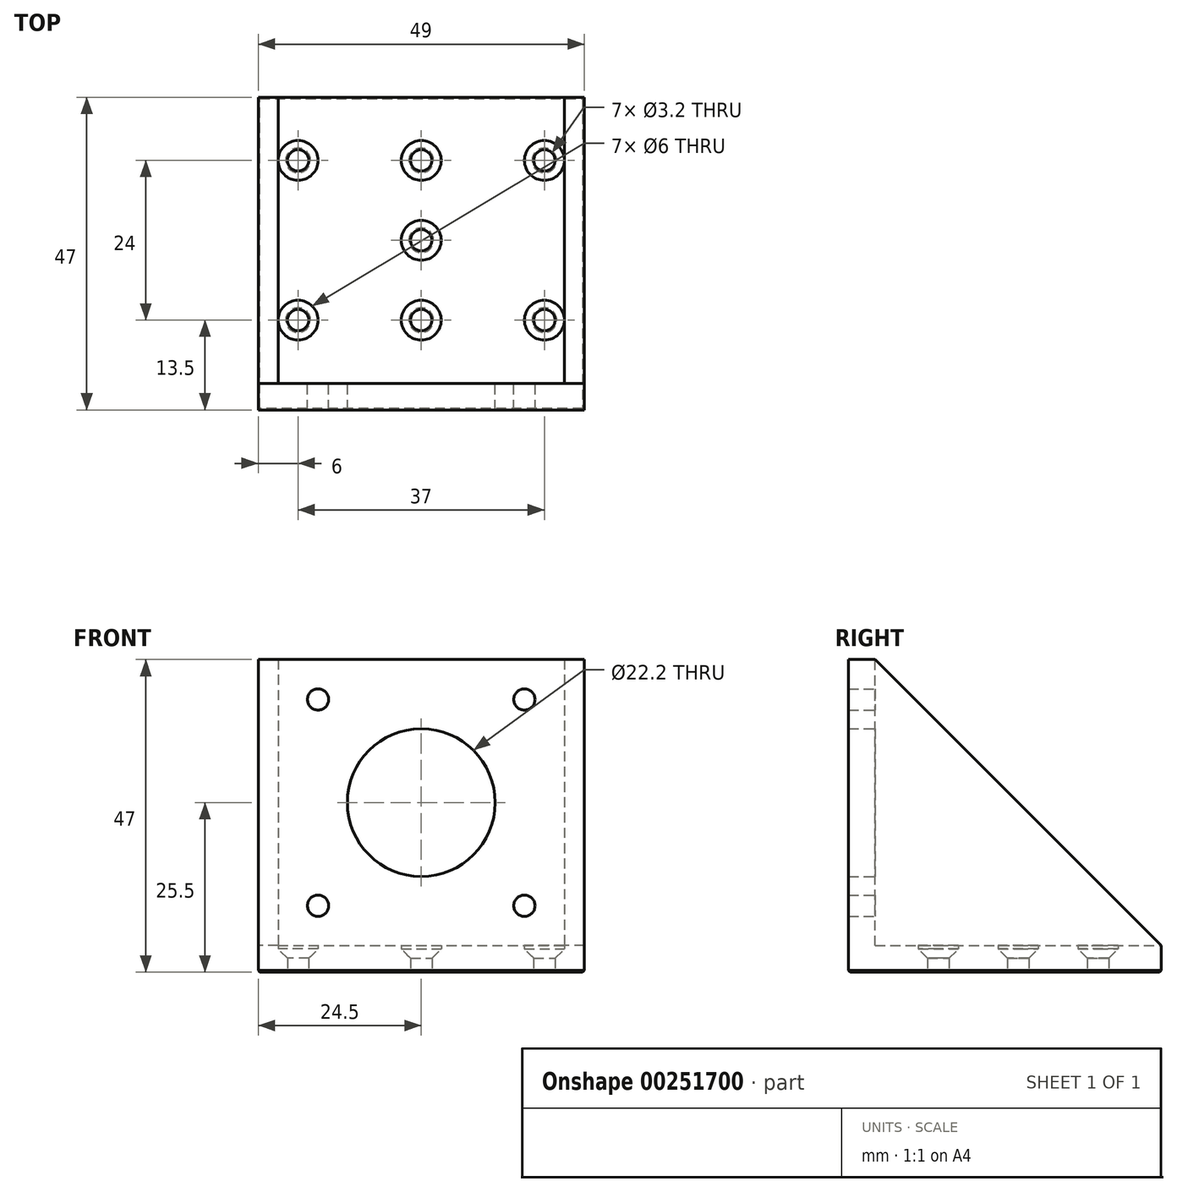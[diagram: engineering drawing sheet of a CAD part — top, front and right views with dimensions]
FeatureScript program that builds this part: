
annotation { "Feature Type Name" : "Feature", "Feature Type Description" : "" }
export const myFeature = defineFeature(function(context is Context, id is Id, definition is map)
    precondition{}
    {
        {
            var Q0;
            Q0=qCreatedBy(makeId("Right.planeOp"),FACE);
            var sketch = newSketch(context, id + "F0", { "sketchPlane" : qUnion([Q0])});
            skLineSegment(sketch, "E0.bottom", {"start": v(-21.5, 0) * mm, "end": v(21.5, 0) * mm});
            skLineSegment(sketch, "E0.top", {"start": v(-21.5, 43) * mm, "end": v(21.5, 43) * mm});
            skLineSegment(sketch, "E0.left", {"start": v(-21.5, 0) * mm, "end": v(-21.5, 43) * mm});
            skLineSegment(sketch, "E0.right", {"start": v(21.5, 0) * mm, "end": v(21.5, 43) * mm});
            skSolve(sketch);
        }
        {
            var Q0;
            Q0=qCreatedBy(makeId("Right.planeOp"),FACE);
            var sketch = newSketch(context, id + "F1", { "sketchPlane" : qUnion([Q0])});
            skLineSegment(sketch, "E1.0", {"start": v(-21.5, 0) * mm, "end": v(-21.5, 43) * mm, "construction": true});
            skLineSegment(sketch, "E2.0", {"start": v(-21.5, 0) * mm, "end": v(21.5, 0) * mm, "construction": true});
            skLineSegment(sketch, "E3", {"start": v(-21.5, 43) * mm, "end": v(21.5, 0) * mm});
            skLineSegment(sketch, "E4", {"start": v(-21.5, 43) * mm, "end": v(-25.5, 43) * mm});
            skLineSegment(sketch, "E5", {"start": v(-25.5, 43) * mm, "end": v(-25.5, -4) * mm});
            skLineSegment(sketch, "E6", {"start": v(-25.5, -4) * mm, "end": v(21.5, -4) * mm});
            skLineSegment(sketch, "E7", {"start": v(21.5, -4) * mm, "end": v(21.5, 0) * mm});
            skPoint(sketch, "E8", {"position": v(-12, 0) * mm});
            skPoint(sketch, "E9", {"position": v(12, 0) * mm});
            skSolve(sketch);
        }
        {
            var Q0;
            Q0 = qSketchRegion(id + "F1", true);
            extrude(context, id + "F2", {"entities" : qUnion([Q0]), "endBound" : BoundingType.SYMMETRIC, "depth" : (43 + 3 + 3) * mm});
        }
        {
            var Q0;
            Q0 = qSketchRegion(id + "F0", true);
            var Q1;
            Q1 = qConstructionFilter(qBodyType(qCreatedBy(id + "F0" ,EDGE), BodyType.WIRE), ConstructionObject.NO);
            extrude(context, id + "F3", {"entities" : qUnion([Q0]), "operationType" : NewBodyOperationType.REMOVE, "surfaceEntities" : qUnion([Q1]), "endBound" : BoundingType.SYMMETRIC, "oppositeDirection" : true, "depth" : 43 * mm});
        }
        {
            var Q0;
            Q0=qCreatedBy(makeId("Front.planeOp"),FACE);
            var sketch = newSketch(context, id + "F13", { "sketchPlane" : qUnion([Q0])});
            skLineSegment(sketch, "E10", {"start": v(0, 0) * mm, "end": v(-3, 0) * mm});
            skLineSegment(sketch, "E11", {"start": v(-3, 0) * mm, "end": v(-3, -0.5) * mm});
            skLineSegment(sketch, "E12", {"start": v(-3, -0.5) * mm, "end": v(-1.6, -1.9) * mm});
            skLineSegment(sketch, "E13", {"start": v(-1.6, -1.9) * mm, "end": v(-1.6, -7.67) * mm});
            skLineSegment(sketch, "E14", {"start": v(-1.6, -7.67) * mm, "end": v(0, -7.67) * mm});
            skLineSegment(sketch, "E15", {"start": v(0, -7.67) * mm, "end": v(0, 0) * mm});
            skSolve(sketch);
        }
        {
            var Q0;
            Q0=makeQuery(id+"F3.boolean.opBoolean","COPY",FACE,{"derivedFrom":makeQuery(id+"F3.opExtrude","SWEPT_FACE",FACE,{"disambiguationData":[OSD([sQuery(id+"F0.wireOp",EDGE,"E0.bottom")])]})});
            var sketch = newSketch(context, id + "F4", { "sketchPlane" : qUnion([Q0])});
            skLineSegment(sketch, "E16.bottom", {"start": v(18.5, 12) * mm, "end": v(-18.5, 12) * mm, "construction": true});
            skLineSegment(sketch, "E16.top", {"start": v(18.5, -12) * mm, "end": v(-18.5, -12) * mm, "construction": true});
            skLineSegment(sketch, "E16.left", {"start": v(18.5, 12) * mm, "end": v(18.5, -12) * mm, "construction": true});
            skLineSegment(sketch, "E16.right", {"start": v(-18.5, 12) * mm, "end": v(-18.5, -12) * mm, "construction": true});
            skPoint(sketch, "E16.middle", {"position": v(0, 0) * mm});
            skCircle(sketch, "E17", {"center": v(18.5, 12) * mm, "radius": 1.6 * mm});
            skCircle(sketch, "E18", {"center": v(-18.5, 12) * mm, "radius": 1.6 * mm});
            skCircle(sketch, "E19", {"center": v(-18.5, -12) * mm, "radius": 1.6 * mm});
            skCircle(sketch, "E20", {"center": v(18.5, -12) * mm, "radius": 1.6 * mm});
            skPoint(sketch, "E21", {"position": v(0, 12) * mm});
            skPoint(sketch, "E22", {"position": v(0, -12) * mm});
            skLineSegment(sketch, "E23", {"start": v(0, 0) * mm, "end": v(0, 12) * mm, "construction": true});
            skLineSegment(sketch, "E24", {"start": v(0, 0) * mm, "end": v(18.5, 0) * mm, "construction": true});
            skLineSegment(sketch, "E25", {"start": v(0, 0) * mm, "end": v(0, -12) * mm, "construction": true});
            skLineSegment(sketch, "E26", {"start": v(0, 0) * mm, "end": v(-18.5, 0) * mm, "construction": true});
            skSolve(sketch);
        }
        {
            var Q0;
            Q0=makeQuery(id+"F3.boolean.opBoolean","COPY",FACE,{"derivedFrom":makeQuery(id+"F3.opExtrude","SWEPT_FACE",FACE,{"disambiguationData":[OSD([sQuery(id+"F0.wireOp",EDGE,"E0.left")])]})});
            var sketch = newSketch(context, id + "F5", { "sketchPlane" : qUnion([Q0])});
            skLineSegment(sketch, "E27", {"start": v(0, 43) * mm, "end": v(0, 0) * mm, "construction": true});
            skLineSegment(sketch, "E28", {"start": v(-21.5, 21.5) * mm, "end": v(21.5, 21.5) * mm, "construction": true});
            skCircle(sketch, "E29", {"center": v(0, 21.5) * mm, "radius": 11.1 * mm});
            skLineSegment(sketch, "E30.bottom", {"start": v(15.5, 37) * mm, "end": v(-15.5, 37) * mm, "construction": true});
            skLineSegment(sketch, "E30.top", {"start": v(15.5, 6) * mm, "end": v(-15.5, 6) * mm, "construction": true});
            skLineSegment(sketch, "E30.left", {"start": v(15.5, 37) * mm, "end": v(15.5, 6) * mm, "construction": true});
            skLineSegment(sketch, "E30.right", {"start": v(-15.5, 37) * mm, "end": v(-15.5, 6) * mm, "construction": true});
            skCircle(sketch, "E31", {"center": v(15.5, 37) * mm, "radius": 1.6 * mm});
            skCircle(sketch, "E32", {"center": v(-15.5, 37) * mm, "radius": 1.6 * mm});
            skCircle(sketch, "E33", {"center": v(-15.5, 6) * mm, "radius": 1.6 * mm});
            skCircle(sketch, "E34", {"center": v(15.5, 6) * mm, "radius": 1.6 * mm});
            skSolve(sketch);
        }
        {
            var Q0;
            Q0 = qSketchRegion(id + "F5", true);
            var Q1;
            Q1=makeQuery(id+"F2.opExtrude","SWEPT_FACE",FACE,{"disambiguationData":[OSD([sQuery(id+"F1.wireOp",EDGE,"E5")])]});
            extrude(context, id + "F6", {"entities" : qUnion([Q0]), "operationType" : NewBodyOperationType.REMOVE, "endBound" : BoundingType.UP_TO_SURFACE, "oppositeDirection" : true, "endBoundEntityFace" : qUnion([Q1]), "depth" : 25 * mm});
        }
        {
            var Q0;
            Q0=makeQuery(id+"F13.imprint","IMPRINT",FACE,{"disambiguationData":[TD([[makeQuery(id+"F13.imprint","IMPRINT",EDGE,{"derivedFrom":sQuery(id+"F13.wireOp",EDGE,"E10")}),1.0]])]});
            var Q1;
            Q1=sQuery(id+"F13.wireOp",EDGE,"E15");
            revolve(context, id + "F7", {"entities" : qUnion([Q0]), "axis" : qUnion([Q1]), "revolveType" : RevolveType.FULL});
        }
        {
            var Q0;
            Q0=makeQuery(id+"F7.opRevolve","SWEPT_BODY",BODY,{"disambiguationData":[OSD([sQuery(id+"F13.wireOp",EDGE,"E10"),sQuery(id+"F13.wireOp",EDGE,"E11"),sQuery(id+"F13.wireOp",EDGE,"E12"),sQuery(id+"F13.wireOp",EDGE,"E13"),sQuery(id+"F13.wireOp",EDGE,"E14"),sQuery(id+"F13.wireOp",EDGE,"E15")])]});
            var Q1;
            Q1=sQuery(id+"F4.wireOp",EDGE,"E23");
            transform(context, id + "F14", {"entities" : qUnion([Q0]), "transformType" : TransformType.TRANSLATION_ENTITY, "oppositeDirectionEntity" : false, "transformLine" : qUnion([Q1]), "makeCopy" : true});
        }
        {
            var Q0;
            Q0=makeQuery(id+"F7.opRevolve","SWEPT_BODY",BODY,{"disambiguationData":[OSD([sQuery(id+"F13.wireOp",EDGE,"E10"),sQuery(id+"F13.wireOp",EDGE,"E11"),sQuery(id+"F13.wireOp",EDGE,"E12"),sQuery(id+"F13.wireOp",EDGE,"E13"),sQuery(id+"F13.wireOp",EDGE,"E14"),sQuery(id+"F13.wireOp",EDGE,"E15")])]});
            var Q1;
            Q1=sQuery(id+"F4.wireOp",EDGE,"E25");
            transform(context, id + "F8", {"entities" : qUnion([Q0]), "transformType" : TransformType.TRANSLATION_ENTITY, "oppositeDirectionEntity" : false, "transformLine" : qUnion([Q1]), "makeCopy" : true});
        }
        {
            var Q0;
            Q0=makeQuery(id+"F14.opPattern","COPY",BODY,{"derivedFrom":makeQuery(id+"F7.opRevolve","SWEPT_BODY",BODY,{"disambiguationData":[OSD([sQuery(id+"F13.wireOp",EDGE,"E10"),sQuery(id+"F13.wireOp",EDGE,"E11"),sQuery(id+"F13.wireOp",EDGE,"E12"),sQuery(id+"F13.wireOp",EDGE,"E13"),sQuery(id+"F13.wireOp",EDGE,"E14"),sQuery(id+"F13.wireOp",EDGE,"E15")])]}),"instanceName":"1"});
            var Q1;
            Q1=sQuery(id+"F4.wireOp",EDGE,"E24");
            transform(context, id + "F9", {"entities" : qUnion([Q0]), "transformType" : TransformType.TRANSLATION_ENTITY, "oppositeDirectionEntity" : false, "transformLine" : qUnion([Q1]), "makeCopy" : true});
        }
        {
            var Q0;
            Q0=makeQuery(id+"F9.opPattern","COPY",BODY,{"derivedFrom":makeQuery(id+"F14.opPattern","COPY",BODY,{"derivedFrom":makeQuery(id+"F7.opRevolve","SWEPT_BODY",BODY,{"disambiguationData":[OSD([sQuery(id+"F13.wireOp",EDGE,"E10"),sQuery(id+"F13.wireOp",EDGE,"E11"),sQuery(id+"F13.wireOp",EDGE,"E12"),sQuery(id+"F13.wireOp",EDGE,"E13"),sQuery(id+"F13.wireOp",EDGE,"E14"),sQuery(id+"F13.wireOp",EDGE,"E15")])]}),"instanceName":"1"}),"instanceName":"1"});
            var Q1;
            Q1=qCreatedBy(makeId("Right.planeOp"),FACE);
            mirror(context, id + "F10", {"entities" : qUnion([Q0]), "mirrorPlane" : qUnion([Q1])});
        }
        {
            var Q0;
            Q0=makeQuery(id+"F9.opPattern","COPY",BODY,{"derivedFrom":makeQuery(id+"F14.opPattern","COPY",BODY,{"derivedFrom":makeQuery(id+"F7.opRevolve","SWEPT_BODY",BODY,{"disambiguationData":[OSD([sQuery(id+"F13.wireOp",EDGE,"E10"),sQuery(id+"F13.wireOp",EDGE,"E11"),sQuery(id+"F13.wireOp",EDGE,"E12"),sQuery(id+"F13.wireOp",EDGE,"E13"),sQuery(id+"F13.wireOp",EDGE,"E14"),sQuery(id+"F13.wireOp",EDGE,"E15")])]}),"instanceName":"1"}),"instanceName":"1"});
            var Q1;
            Q1=makeQuery(id+"F10.opPattern","COPY",BODY,{"derivedFrom":makeQuery(id+"F9.opPattern","COPY",BODY,{"derivedFrom":makeQuery(id+"F14.opPattern","COPY",BODY,{"derivedFrom":makeQuery(id+"F7.opRevolve","SWEPT_BODY",BODY,{"disambiguationData":[OSD([sQuery(id+"F13.wireOp",EDGE,"E10"),sQuery(id+"F13.wireOp",EDGE,"E11"),sQuery(id+"F13.wireOp",EDGE,"E12"),sQuery(id+"F13.wireOp",EDGE,"E13"),sQuery(id+"F13.wireOp",EDGE,"E14"),sQuery(id+"F13.wireOp",EDGE,"E15")])]}),"instanceName":"1"}),"instanceName":"1"}),"instanceName":"1"});
            var Q2;
            Q2=qCreatedBy(makeId("Front.planeOp"),FACE);
            mirror(context, id + "F15", {"entities" : qUnion([Q0, Q1]), "mirrorPlane" : qUnion([Q2])});
        }
        {
            var Q0;
            Q0=makeQuery(id+"F15.opPattern","COPY",BODY,{"derivedFrom":makeQuery(id+"F9.opPattern","COPY",BODY,{"derivedFrom":makeQuery(id+"F14.opPattern","COPY",BODY,{"derivedFrom":makeQuery(id+"F7.opRevolve","SWEPT_BODY",BODY,{"disambiguationData":[OSD([sQuery(id+"F13.wireOp",EDGE,"E10"),sQuery(id+"F13.wireOp",EDGE,"E11"),sQuery(id+"F13.wireOp",EDGE,"E12"),sQuery(id+"F13.wireOp",EDGE,"E13"),sQuery(id+"F13.wireOp",EDGE,"E14"),sQuery(id+"F13.wireOp",EDGE,"E15")])]}),"instanceName":"1"}),"instanceName":"1"}),"instanceName":"1"});
            var Q1;
            Q1=makeQuery(id+"F8.opPattern","COPY",BODY,{"derivedFrom":makeQuery(id+"F7.opRevolve","SWEPT_BODY",BODY,{"disambiguationData":[OSD([sQuery(id+"F13.wireOp",EDGE,"E10"),sQuery(id+"F13.wireOp",EDGE,"E11"),sQuery(id+"F13.wireOp",EDGE,"E12"),sQuery(id+"F13.wireOp",EDGE,"E13"),sQuery(id+"F13.wireOp",EDGE,"E14"),sQuery(id+"F13.wireOp",EDGE,"E15")])]}),"instanceName":"1"});
            var Q2;
            Q2=makeQuery(id+"F15.opPattern","COPY",BODY,{"derivedFrom":makeQuery(id+"F10.opPattern","COPY",BODY,{"derivedFrom":makeQuery(id+"F9.opPattern","COPY",BODY,{"derivedFrom":makeQuery(id+"F14.opPattern","COPY",BODY,{"derivedFrom":makeQuery(id+"F7.opRevolve","SWEPT_BODY",BODY,{"disambiguationData":[OSD([sQuery(id+"F13.wireOp",EDGE,"E10"),sQuery(id+"F13.wireOp",EDGE,"E11"),sQuery(id+"F13.wireOp",EDGE,"E12"),sQuery(id+"F13.wireOp",EDGE,"E13"),sQuery(id+"F13.wireOp",EDGE,"E14"),sQuery(id+"F13.wireOp",EDGE,"E15")])]}),"instanceName":"1"}),"instanceName":"1"}),"instanceName":"1"}),"instanceName":"1"});
            var Q3;
            Q3=makeQuery(id+"F9.opPattern","COPY",BODY,{"derivedFrom":makeQuery(id+"F14.opPattern","COPY",BODY,{"derivedFrom":makeQuery(id+"F7.opRevolve","SWEPT_BODY",BODY,{"disambiguationData":[OSD([sQuery(id+"F13.wireOp",EDGE,"E10"),sQuery(id+"F13.wireOp",EDGE,"E11"),sQuery(id+"F13.wireOp",EDGE,"E12"),sQuery(id+"F13.wireOp",EDGE,"E13"),sQuery(id+"F13.wireOp",EDGE,"E14"),sQuery(id+"F13.wireOp",EDGE,"E15")])]}),"instanceName":"1"}),"instanceName":"1"});
            var Q4;
            Q4=makeQuery(id+"F14.opPattern","COPY",BODY,{"derivedFrom":makeQuery(id+"F7.opRevolve","SWEPT_BODY",BODY,{"disambiguationData":[OSD([sQuery(id+"F13.wireOp",EDGE,"E10"),sQuery(id+"F13.wireOp",EDGE,"E11"),sQuery(id+"F13.wireOp",EDGE,"E12"),sQuery(id+"F13.wireOp",EDGE,"E13"),sQuery(id+"F13.wireOp",EDGE,"E14"),sQuery(id+"F13.wireOp",EDGE,"E15")])]}),"instanceName":"1"});
            var Q5;
            Q5=makeQuery(id+"F10.opPattern","COPY",BODY,{"derivedFrom":makeQuery(id+"F9.opPattern","COPY",BODY,{"derivedFrom":makeQuery(id+"F14.opPattern","COPY",BODY,{"derivedFrom":makeQuery(id+"F7.opRevolve","SWEPT_BODY",BODY,{"disambiguationData":[OSD([sQuery(id+"F13.wireOp",EDGE,"E10"),sQuery(id+"F13.wireOp",EDGE,"E11"),sQuery(id+"F13.wireOp",EDGE,"E12"),sQuery(id+"F13.wireOp",EDGE,"E13"),sQuery(id+"F13.wireOp",EDGE,"E14"),sQuery(id+"F13.wireOp",EDGE,"E15")])]}),"instanceName":"1"}),"instanceName":"1"}),"instanceName":"1"});
            var Q6;
            Q6=makeQuery(id+"F7.opRevolve","SWEPT_BODY",BODY,{"disambiguationData":[OSD([sQuery(id+"F13.wireOp",EDGE,"E10"),sQuery(id+"F13.wireOp",EDGE,"E11"),sQuery(id+"F13.wireOp",EDGE,"E12"),sQuery(id+"F13.wireOp",EDGE,"E13"),sQuery(id+"F13.wireOp",EDGE,"E14"),sQuery(id+"F13.wireOp",EDGE,"E15")])]});
            var Q7;
            Q7=makeQuery(id+"F2.opExtrude","SWEPT_BODY",BODY,{"disambiguationData":[OSD([sQuery(id+"F1.wireOp",EDGE,"E3"),sQuery(id+"F1.wireOp",EDGE,"E4"),sQuery(id+"F1.wireOp",EDGE,"E5"),sQuery(id+"F1.wireOp",EDGE,"E6"),sQuery(id+"F1.wireOp",EDGE,"E7")])]});
            booleanBodies(context, id + "F11", {"operationType" : BooleanOperationType.SUBTRACTION, "tools" : qUnion([Q0, Q1, Q2, Q3, Q4, Q5, Q6]), "targets" : qUnion([Q7])});
        }
        {
            var Q0;
            Q0=makeQuery(id+"F2.opExtrude","SWEPT_FACE",FACE,{"disambiguationData":[OSD([sQuery(id+"F1.wireOp",EDGE,"E6")])]});
            chamfer(context, id + "F12", {"entities" : qUnion([Q0]), "width" : 0.25 * mm});
        }
    });
